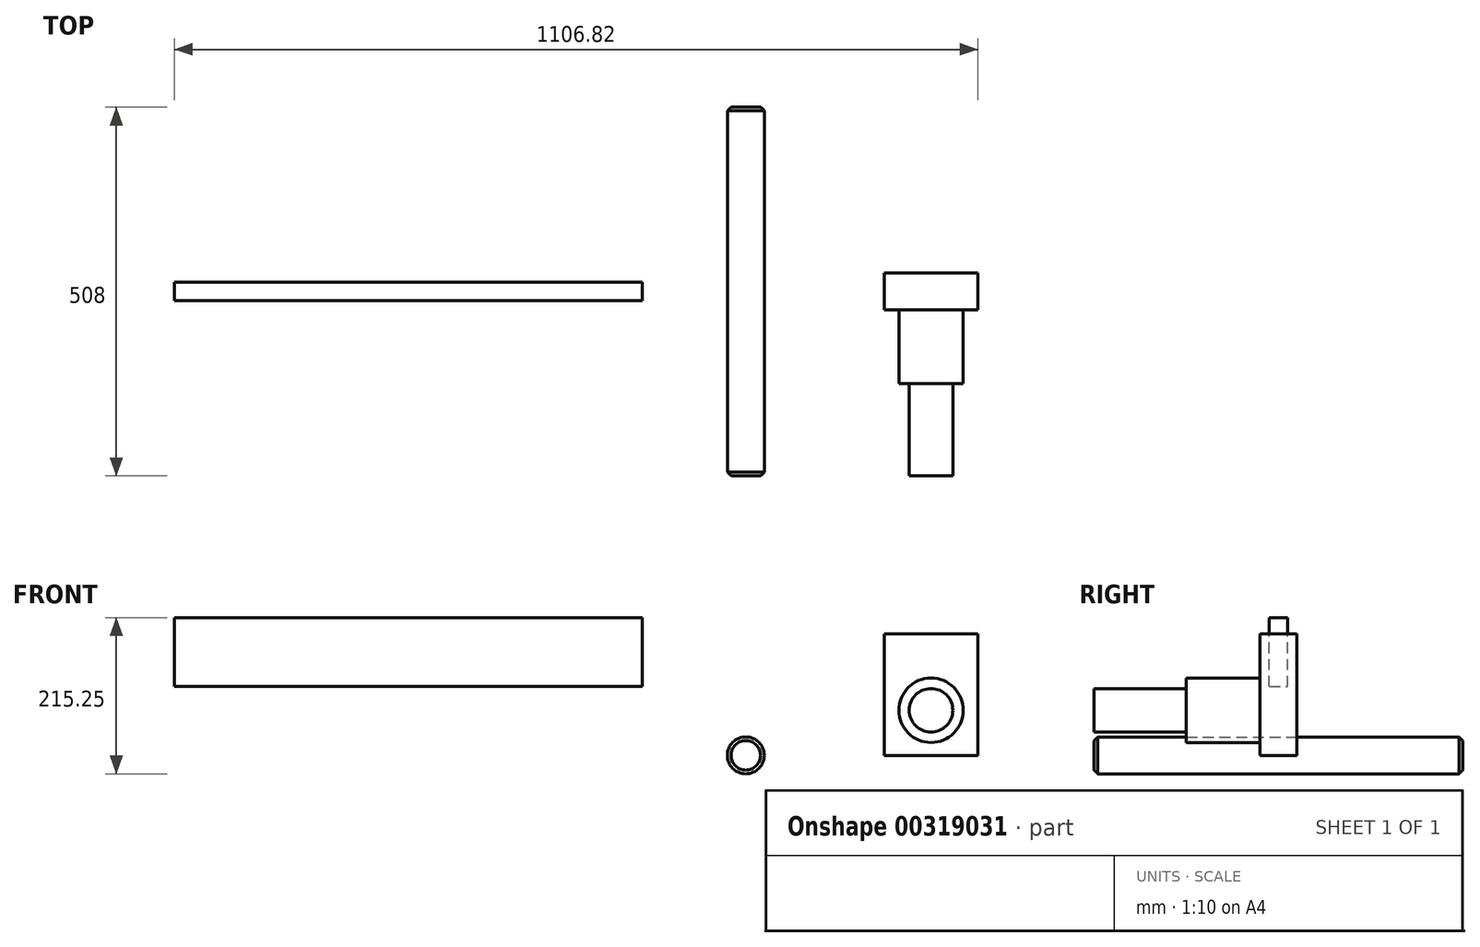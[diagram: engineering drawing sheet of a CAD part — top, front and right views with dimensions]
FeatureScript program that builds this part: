
annotation { "Feature Type Name" : "Feature", "Feature Type Description" : "" }
export const myFeature = defineFeature(function(context is Context, id is Id, definition is map)
    precondition{}
    {
        {
            var Q0;
            Q0=qCreatedBy(makeId("Front.planeOp"),FACE);
            var sketch = newSketch(context, id + "F0", { "sketchPlane" : qUnion([Q0])});
            skCircle(sketch, "E0", {"center": v(0, 0) * mm, "radius": 25.4 * mm});
            skSolve(sketch);
        }
        {
            var Q0;
            Q0=makeQuery(id+"F0.imprint","IMPRINT",FACE,{"disambiguationData":[TD([[makeQuery(id+"F0.imprint","IMPRINT",EDGE,{"derivedFrom":sQuery(id+"F0.wireOp",EDGE,"E0")}),1.0]])]});
            extrude(context, id + "F1", {"entities" : qUnion([Q0]), "endBound" : BoundingType.SYMMETRIC, "depth" : 508 * mm});
        }
        {
            var Q0;
            Q0=makeQuery(id+"F1.opExtrude","CAP_EDGE",EDGE,{"disambiguationData":[OSD([sQuery(id+"F0.wireOp",EDGE,"E0")])],"isStart":true});
            var Q1;
            Q1=makeQuery(id+"F1.opExtrude","CAP_EDGE",EDGE,{"disambiguationData":[OSD([sQuery(id+"F0.wireOp",EDGE,"E0")])],"isStart":false});
            chamfer(context, id + "F2", {"entities" : qUnion([Q0, Q1]), "width" : 5.08 * mm, "tangentPropagation" : true});
        }
        {
            var Q0;
            Q0=qCreatedBy(makeId("Front.planeOp"),FACE);
            var sketch = newSketch(context, id + "F3", { "sketchPlane" : qUnion([Q0])});
            skLineSegment(sketch, "E1.bottom", {"start": v(190.68, 0) * mm, "end": v(319.66, 0) * mm});
            skLineSegment(sketch, "E1.top", {"start": v(190.68, 167.54) * mm, "end": v(319.66, 167.54) * mm});
            skLineSegment(sketch, "E1.left", {"start": v(190.68, 0) * mm, "end": v(190.68, 167.54) * mm});
            skLineSegment(sketch, "E1.right", {"start": v(319.66, 0) * mm, "end": v(319.66, 167.54) * mm});
            skPoint(sketch, "E1.middle", {"position": v(255.17, 83.77) * mm});
            skCircle(sketch, "E2", {"center": v(255.17, 62.04) * mm, "radius": 44.34 * mm});
            skCircle(sketch, "E3", {"center": v(255.17, 62.04) * mm, "radius": 30 * mm});
            skSolve(sketch);
        }
        {
            var Q0;
            Q0=makeQuery(id+"F3.imprint","IMPRINT",FACE,{"disambiguationData":[TD([[makeQuery(id+"F3.imprint","IMPRINT",EDGE,{"derivedFrom":sQuery(id+"F3.wireOp",EDGE,"E1.bottom")}),1.0]])]});
            extrude(context, id + "F4", {"entities" : qUnion([Q0]), "endBound" : BoundingType.SYMMETRIC, "depth" : 50.8 * mm});
        }
        {
            var Q0;
            Q0=makeQuery(id+"F3.imprint","IMPRINT",FACE,{"disambiguationData":[TD([[makeQuery(id+"F3.imprint","IMPRINT",EDGE,{"derivedFrom":sQuery(id+"F3.wireOp",EDGE,"E2")}),1.0]])]});
            extrude(context, id + "F5", {"entities" : qUnion([Q0]), "operationType" : NewBodyOperationType.ADD, "depth" : 127 * mm, "hasSecondDirection" : true, "secondDirectionOppositeDirection" : true, "secondDirectionDepth" : 25.4 * mm});
        }
        {
            var Q0;
            Q0=makeQuery(id+"F3.imprint","IMPRINT",FACE,{"disambiguationData":[TD([[makeQuery(id+"F3.imprint","IMPRINT",EDGE,{"derivedFrom":sQuery(id+"F3.wireOp",EDGE,"E3")}),1.0]])]});
            extrude(context, id + "F6", {"entities" : qUnion([Q0]), "operationType" : NewBodyOperationType.ADD, "depth" : 254 * mm, "hasSecondDirection" : true, "secondDirectionOppositeDirection" : true, "secondDirectionDepth" : 25.4 * mm});
        }
        {
            var Q0;
            Q0=qCreatedBy(makeId("Front.planeOp"),FACE);
            var sketch = newSketch(context, id + "F7", { "sketchPlane" : qUnion([Q0])});
            skLineSegment(sketch, "E4.bottom", {"start": v(-142.76, 94.68) * mm, "end": v(-787.16, 94.68) * mm});
            skLineSegment(sketch, "E4.top", {"start": v(-142.76, 189.85) * mm, "end": v(-787.16, 189.85) * mm});
            skLineSegment(sketch, "E4.left", {"start": v(-142.76, 94.68) * mm, "end": v(-142.76, 189.85) * mm});
            skLineSegment(sketch, "E4.right", {"start": v(-787.16, 94.68) * mm, "end": v(-787.16, 189.85) * mm});
            skPoint(sketch, "E4.middle", {"position": v(-464.96, 142.26) * mm});
            skSolve(sketch);
        }
        {
            var Q0;
            Q0=makeQuery(id+"F7.imprint","IMPRINT",FACE,{"disambiguationData":[TD([[makeQuery(id+"F7.imprint","IMPRINT",EDGE,{"derivedFrom":sQuery(id+"F7.wireOp",EDGE,"E4.bottom")}),-1.0]])]});
            extrude(context, id + "F8", {"entities" : qUnion([Q0]), "endBound" : BoundingType.SYMMETRIC, "depth" : 25.4 * mm});
        }
    });
